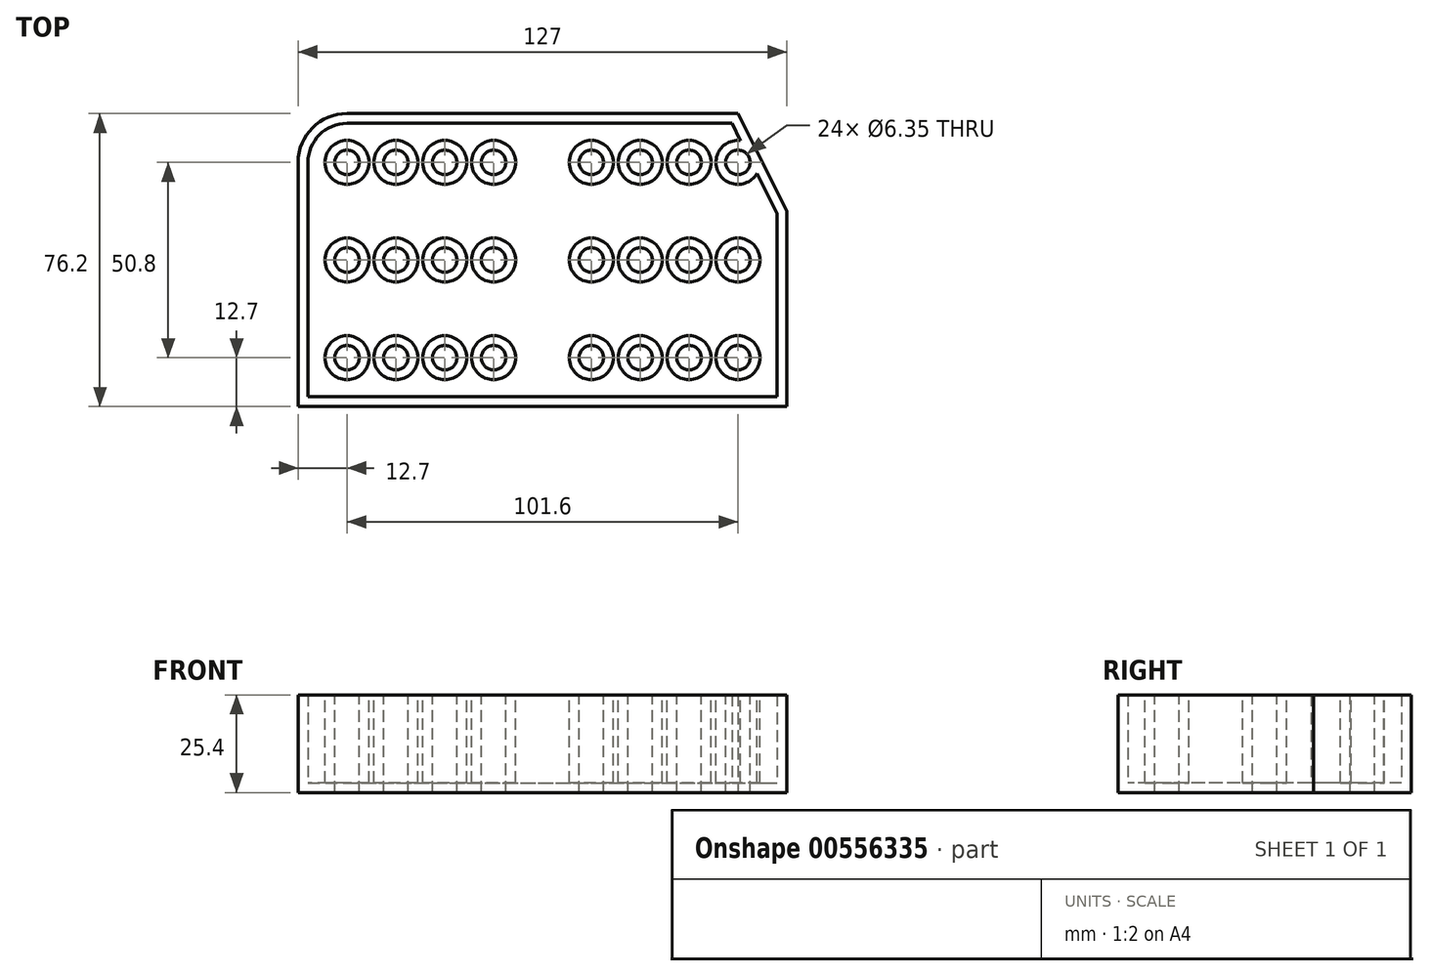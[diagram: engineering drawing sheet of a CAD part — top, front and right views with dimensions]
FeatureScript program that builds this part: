
annotation { "Feature Type Name" : "Feature", "Feature Type Description" : "" }
export const myFeature = defineFeature(function(context is Context, id is Id, definition is map)
    precondition{}
    {
        {
            var Q0;
            Q0=qCreatedBy(makeId("Top.planeOp"),FACE);
            var sketch = newSketch(context, id + "F0", { "sketchPlane" : qUnion([Q0])});
            skLineSegment(sketch, "E0.bottom", {"start": v(-50.8, 38.1) * mm, "end": v(50.8, 38.1) * mm});
            skLineSegment(sketch, "E0.top", {"start": v(-63.5, -38.1) * mm, "end": v(63.5, -38.1) * mm});
            skLineSegment(sketch, "E0.left", {"start": v(-63.5, 25.4) * mm, "end": v(-63.5, -38.1) * mm});
            skLineSegment(sketch, "E0.right", {"start": v(63.5, 12.7) * mm, "end": v(63.5, -38.1) * mm});
            skPoint(sketch, "E0.middle", {"position": v(0, 0) * mm});
            skPoint(sketch, "E1.visualSharp", {"position": v(-63.5, 38.1) * mm});
            skArc(sketch, "E1.filletArc", {"start": v(-50.8, 38.1) * mm, "mid": v(-59.78, 34.38) * mm, "end": v(-63.5, 25.4) * mm});
            skLineSegment(sketch, "E2", {"start": v(50.8, 38.1) * mm, "end": v(63.5, 12.7) * mm});
            skPoint(sketch, "E3.orphan", {"position": v(63.5, 38.1) * mm});
            skSolve(sketch);
        }
        {
            var Q0;
            Q0=makeQuery(id+"F0.imprint","IMPRINT",FACE,{"disambiguationData":[TD([[makeQuery(id+"F0.imprint","IMPRINT",EDGE,{"derivedFrom":sQuery(id+"F0.wireOp",EDGE,"E0.bottom")}),-1.0]])]});
            extrude(context, id + "F1", {"entities" : qUnion([Q0]), "depth" : 25.4 * mm, "offsetDistance" : 25.4 * mm});
        }
        {
            var Q0;
            Q0=makeQuery(id+"F1.opExtrude","CAP_FACE",FACE,{"disambiguationData":[OSD([sQuery(id+"F0.wireOp",EDGE,"E0.bottom"),sQuery(id+"F0.wireOp",EDGE,"E0.top"),sQuery(id+"F0.wireOp",EDGE,"E0.left"),sQuery(id+"F0.wireOp",EDGE,"E0.right"),sQuery(id+"F0.wireOp",EDGE,"E1.filletArc"),sQuery(id+"F0.wireOp",EDGE,"E2")])],"isStart":false});
            var sketch = newSketch(context, id + "F2", { "sketchPlane" : qUnion([Q0])});
            skCircle(sketch, "E4", {"center": v(-46.03, -88.9) * mm, "radius": 32.9 * mm});
            skSolve(sketch);
        }
        {
            var Q0;
            Q0=makeQuery(id+"F2.imprint","IMPRINT",FACE,{"disambiguationData":[TD([[makeQuery(id+"F2.imprint","IMPRINT",EDGE,{"derivedFrom":makeQuery(id+"F1.opExtrude","CAP_EDGE",EDGE,{"disambiguationData":[OSD([sQuery(id+"F0.wireOp",EDGE,"E0.bottom")])],"isStart":false})}),-1.0]])]});
            var sketch = newSketch(context, id + "F3", { "sketchPlane" : qUnion([Q0])});
            skCircle(sketch, "E5", {"center": v(-50.8, 25.4) * mm, "radius": 3.18 * mm});
            skCircle(sketch, "E6.0.1.0", {"center": v(-50.8, 0) * mm, "radius": 3.18 * mm});
            skCircle(sketch, "E6.0.2.0", {"center": v(-50.8, -25.4) * mm, "radius": 3.18 * mm});
            skCircle(sketch, "E6.1.0.0", {"center": v(-38.1, 25.4) * mm, "radius": 3.18 * mm});
            skCircle(sketch, "E6.1.1.0", {"center": v(-38.1, 0) * mm, "radius": 3.18 * mm});
            skCircle(sketch, "E6.1.2.0", {"center": v(-38.1, -25.4) * mm, "radius": 3.18 * mm});
            skCircle(sketch, "E6.2.0.0", {"center": v(-25.4, 25.4) * mm, "radius": 3.18 * mm});
            skCircle(sketch, "E6.2.1.0", {"center": v(-25.4, 0) * mm, "radius": 3.18 * mm});
            skCircle(sketch, "E6.2.2.0", {"center": v(-25.4, -25.4) * mm, "radius": 3.18 * mm});
            skCircle(sketch, "E6.3.0.0", {"center": v(-12.7, 25.4) * mm, "radius": 3.18 * mm});
            skCircle(sketch, "E6.3.1.0", {"center": v(-12.7, 0) * mm, "radius": 3.18 * mm});
            skCircle(sketch, "E6.3.2.0", {"center": v(-12.7, -25.4) * mm, "radius": 3.18 * mm});
            skLineSegment(sketch, "E6.direction1", {"start": v(-50.8, 25.4) * mm, "end": v(-38.1, 25.4) * mm, "construction": true});
            skLineSegment(sketch, "E6.direction2", {"start": v(-50.8, 25.4) * mm, "end": v(-50.8, 0) * mm, "construction": true});
            skLineSegment(sketch, "E7", {"start": v(0, 33.9) * mm, "end": v(0, -23.99) * mm, "construction": true});
            skCircle(sketch, "E8.MirrorC", {"center": v(50.8, 25.4) * mm, "radius": 3.18 * mm});
            skCircle(sketch, "E9.MirrorC", {"center": v(38.1, 25.4) * mm, "radius": 3.18 * mm});
            skCircle(sketch, "E10.MirrorC", {"center": v(25.4, 25.4) * mm, "radius": 3.18 * mm});
            skCircle(sketch, "E11.MirrorC", {"center": v(12.7, 25.4) * mm, "radius": 3.18 * mm});
            skCircle(sketch, "E12.MirrorC", {"center": v(12.7, 0) * mm, "radius": 3.18 * mm});
            skCircle(sketch, "E13.MirrorC", {"center": v(25.4, 0) * mm, "radius": 3.18 * mm});
            skCircle(sketch, "E14.MirrorC", {"center": v(38.1, 0) * mm, "radius": 3.18 * mm});
            skCircle(sketch, "E15.MirrorC", {"center": v(50.8, -25.4) * mm, "radius": 3.18 * mm});
            skCircle(sketch, "E16.MirrorC", {"center": v(38.1, -25.4) * mm, "radius": 3.18 * mm});
            skCircle(sketch, "E17.MirrorC", {"center": v(25.4, -25.4) * mm, "radius": 3.18 * mm});
            skCircle(sketch, "E18.MirrorC", {"center": v(12.7, -25.4) * mm, "radius": 3.18 * mm});
            skCircle(sketch, "E19.MirrorC", {"center": v(50.8, 0) * mm, "radius": 3.18 * mm});
            skSolve(sketch);
        }
        {
            var Q0;
            Q0 = qSketchRegion(id + "F3", true);
            extrude(context, id + "F4", {"entities" : qUnion([Q0]), "operationType" : NewBodyOperationType.REMOVE, "oppositeDirection" : true, "depth" : 25.4 * mm, "offsetDistance" : 25.4 * mm});
        }
        {
            var Q0;
            Q0=makeQuery(id+"F1.opExtrude","CAP_FACE",FACE,{"disambiguationData":[OSD([sQuery(id+"F0.wireOp",EDGE,"E0.bottom"),sQuery(id+"F0.wireOp",EDGE,"E0.top"),sQuery(id+"F0.wireOp",EDGE,"E0.left"),sQuery(id+"F0.wireOp",EDGE,"E0.right"),sQuery(id+"F0.wireOp",EDGE,"E1.filletArc"),sQuery(id+"F0.wireOp",EDGE,"E2")])],"isStart":false});
            shell(context, id + "F5", {"entities" : qUnion([Q0]), "thickness" : 2.54 * mm});
        }
    });
